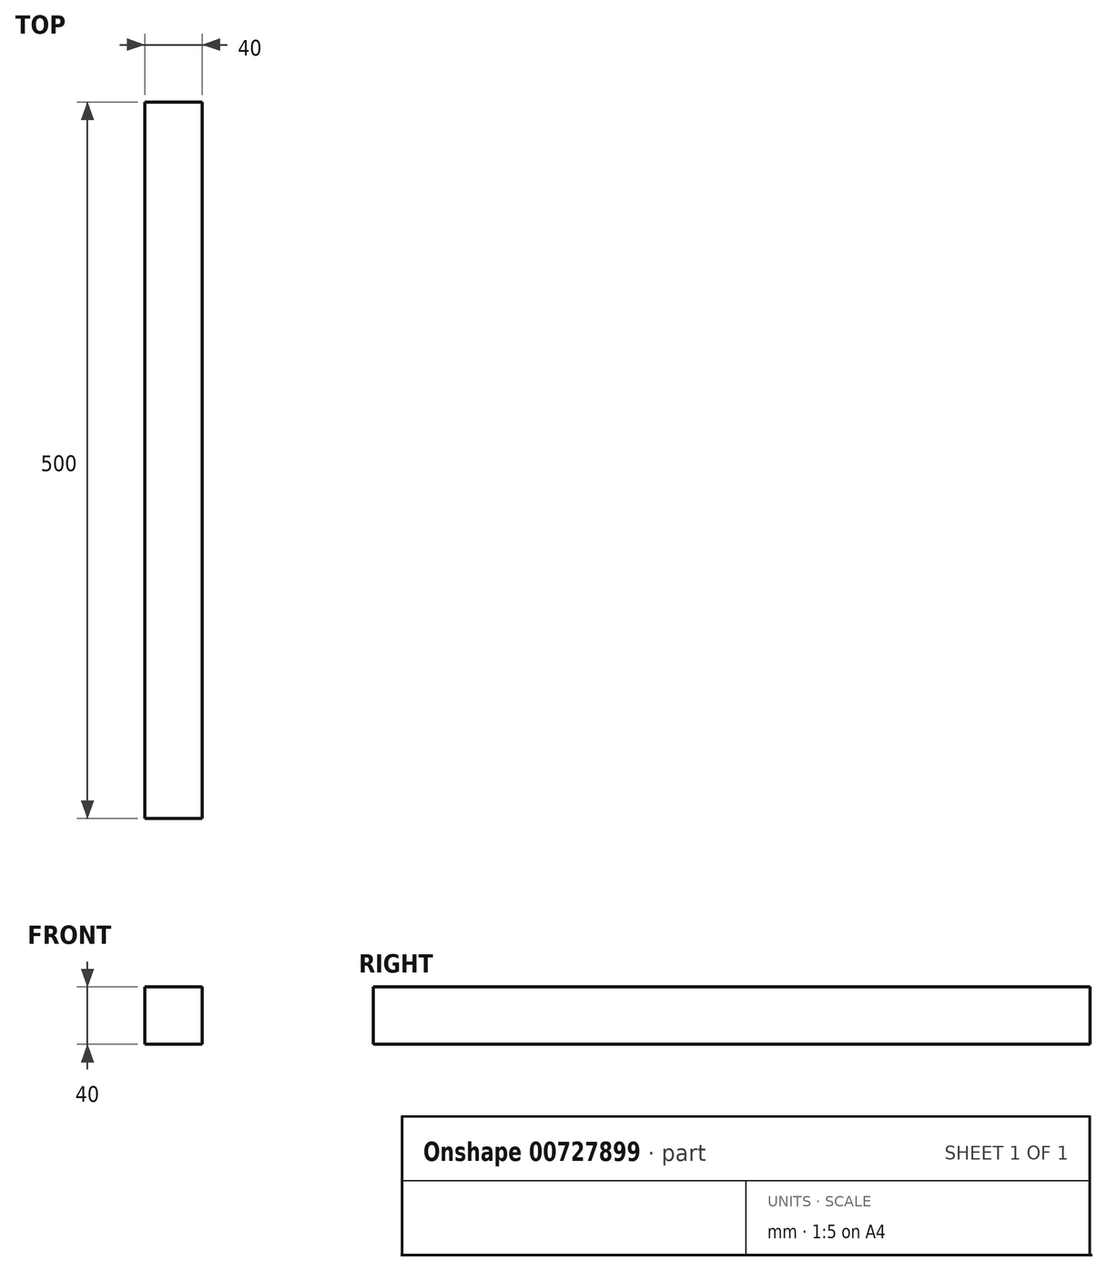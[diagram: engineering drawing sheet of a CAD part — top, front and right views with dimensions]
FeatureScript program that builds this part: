
annotation { "Feature Type Name" : "Feature", "Feature Type Description" : "" }
export const myFeature = defineFeature(function(context is Context, id is Id, definition is map)
    precondition{}
    {
        {
            var Q0;
            Q0=qCreatedBy(makeId("Right.planeOp"),FACE);
            var sketch = newSketch(context, id + "F0", { "sketchPlane" : qUnion([Q0])});
            skLineSegment(sketch, "E0.bottom", {"start": v(-242.58, 0) * mm, "end": v(257.42, 0) * mm});
            skLineSegment(sketch, "E0.top", {"start": v(-242.58, -40) * mm, "end": v(257.42, -40) * mm});
            skLineSegment(sketch, "E0.left", {"start": v(-242.58, 0) * mm, "end": v(-242.58, -40) * mm});
            skLineSegment(sketch, "E0.right", {"start": v(257.42, 0) * mm, "end": v(257.42, -40) * mm});
            skSolve(sketch);
        }
        {
            var Q0;
            Q0 = qSketchRegion(id + "F0", true);
            extrude(context, id + "F1", {"entities" : qUnion([Q0]), "endBound" : BoundingType.SYMMETRIC, "depth" : 40 * mm, "offsetDistance" : 25 * mm});
        }
    });
